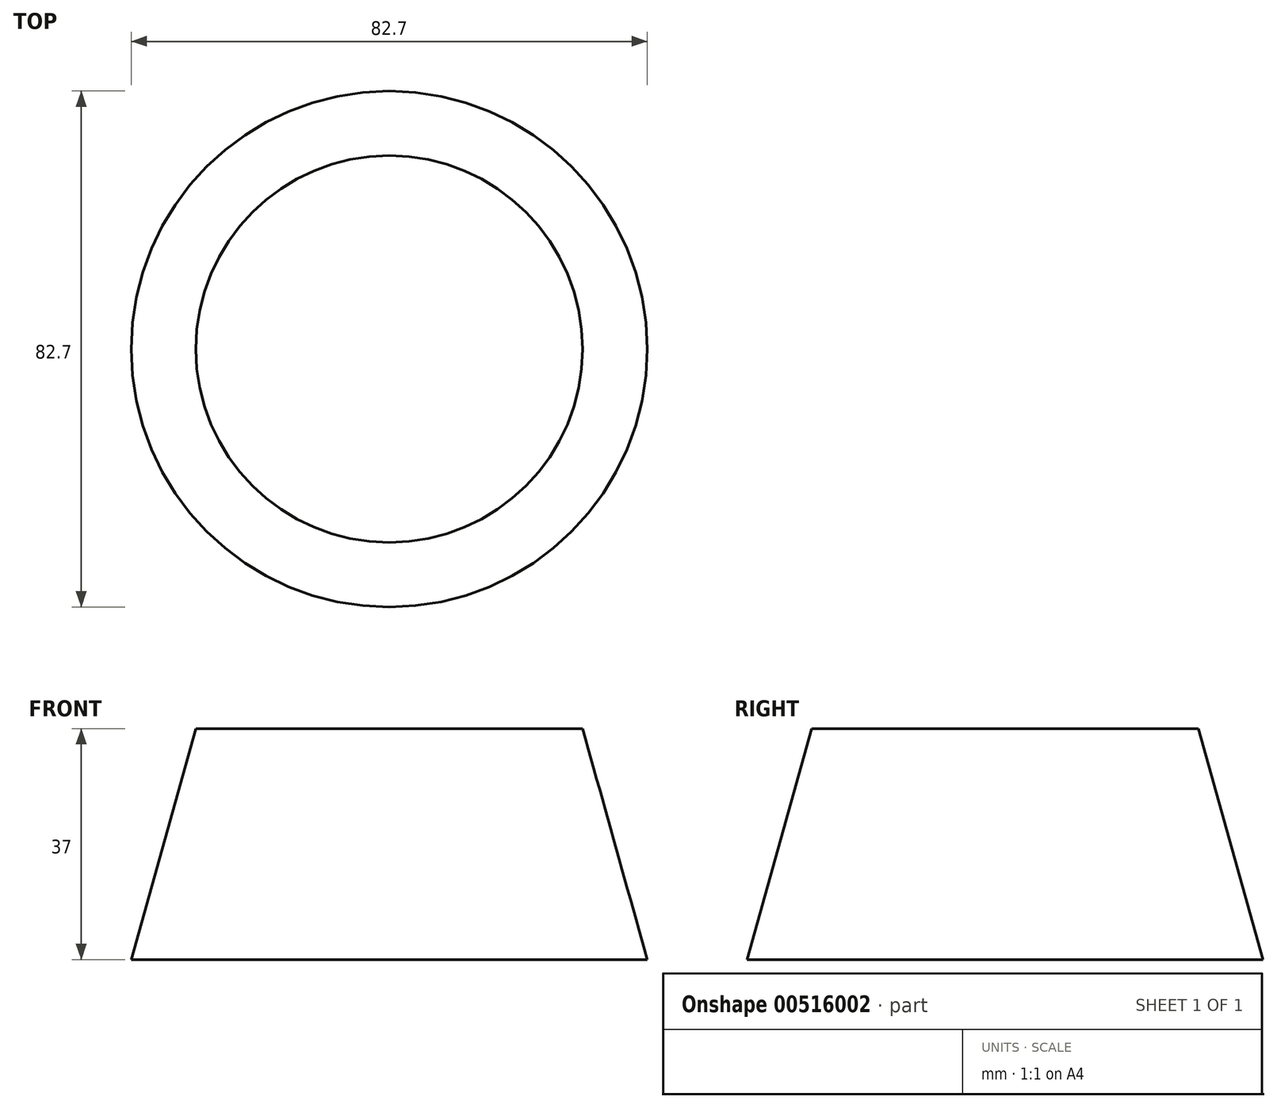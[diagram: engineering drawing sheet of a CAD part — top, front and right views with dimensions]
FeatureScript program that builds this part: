
annotation { "Feature Type Name" : "Feature", "Feature Type Description" : "" }
export const myFeature = defineFeature(function(context is Context, id is Id, definition is map)
    precondition{}
    {
        {
            var Q0;
            Q0=qCreatedBy(makeId("Top.planeOp"),FACE);
            var sketch = newSketch(context, id + "F0", { "sketchPlane" : qUnion([Q0])});
            skCircle(sketch, "E0", {"center": v(0, 0) * mm, "radius": 41.35 * mm});
            skSolve(sketch);
        }
        {
            var Q0;
            Q0=qCreatedBy(makeId("Top.planeOp"),FACE);
            cPlane(context, id + "F1", {"entities" : qUnion([Q0]), "cplaneType" : CPlaneType.OFFSET, "offset" : 37 * mm, "width" : 150 * mm, "height" : 150 * mm});
        }
        {
            var Q0;
            Q0=qCreatedBy(id+"F1.planeOp",FACE);
            var sketch = newSketch(context, id + "F2", { "sketchPlane" : qUnion([Q0])});
            skCircle(sketch, "E1", {"center": v(0, 0) * mm, "radius": 31 * mm});
            skSolve(sketch);
        }
        {
            var Q0;
            Q0=qCreatedBy(makeId("Front.planeOp"),FACE);
            var sketch = newSketch(context, id + "F3", { "sketchPlane" : qUnion([Q0])});
            skLineSegment(sketch, "E2.0", {"start": v(-31, 37) * mm, "end": v(0, 37) * mm, "construction": true});
            skLineSegment(sketch, "E3", {"start": v(0, 37) * mm, "end": v(0, 0) * mm});
            skLineSegment(sketch, "E4", {"start": v(0, 37) * mm, "end": v(-31, 37) * mm});
            skLineSegment(sketch, "E5.0", {"start": v(-41.35, 0) * mm, "end": v(0, 0) * mm});
            skLineSegment(sketch, "E6", {"start": v(-31, 37) * mm, "end": v(-41.35, 0) * mm});
            skPoint(sketch, "E7.orphan", {"position": v(31, 37) * mm});
            skPoint(sketch, "E8.orphan", {"position": v(41.35, 0) * mm});
            skSolve(sketch);
        }
        {
            var Q0;
            Q0=makeQuery(id+"F3.imprint","IMPRINT",FACE,{"disambiguationData":[TD([[makeQuery(id+"F3.imprint","IMPRINT",EDGE,{"derivedFrom":sQuery(id+"F3.wireOp",EDGE,"E3")}),-1.0]])]});
            var Q1;
            Q1=sQuery(id+"F3.wireOp",EDGE,"E3");
            revolve(context, id + "F4", {"entities" : qUnion([Q0]), "axis" : qUnion([Q1]), "revolveType" : RevolveType.FULL});
        }
    });
